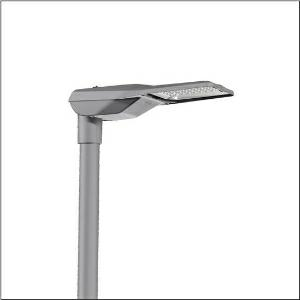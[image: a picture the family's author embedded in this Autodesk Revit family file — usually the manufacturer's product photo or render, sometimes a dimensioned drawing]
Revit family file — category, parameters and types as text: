
# Revit family: streetlight_sl_21_mini___st0_5a_5xe2b43s08gb_d1ce
name_source: partatom
category: Lighting Fixtures
units: mm (PartAtom-declared; Revit-internal decimal feet)

## family parameters
Cut with Voids When Loaded = No
Host = Face
Light Source = No
Part Type = Normal
Room Calculation Point = No
Round Connector Dimension = Use Diameter
Shared = No

## types (1)
- --- (1 x LED, 6180 lm, 40.4 W, 4000K)
    Apparent Load = 40 VA
    CIE Flux Codes = 41 75 97 100 100
    Color Rendering = 70
    Color Temperature = 4000K
    Default Elevation = 1800 mm
    Description = Streetlight SL 21 mini, mast luminaire, primary light control with lens, of PMMA, primary optical cover: cover, of toughened safety glass, transparent, light distribution: ST0.5a, light emission: direct distribution, primary light characteristic: asymmetric, installation type: side-entry, post-top, LED, High Power LED, rated luminous flux: 6.180lm, luminous efficacy: 153lm/W, light colour: 740, colour temperature: 4000K, control gear: ECG Smart Interface, control: overheat protection, constant luminous flux control, time-dependent luminous flux control, flexible luminous flux parameterisation, mains connection: 220..240V, AC, 50/60Hz, start of lifetime: 40W, end of lifetime: 41W, reduction: 19W, luminaire housing, of diecast aluminium, powder-coated, Siteco® metallic grey (DB 702S), corrosivity category C5 according to DIN EN ISO 12944, length: 628mm, width: 235mm, height: 110mm, spigot size: 60/76mm (post-top) and 42/60/76mm (side-entry), mast flange for spigot size: 42mm: 5XC10008XM4, 60mm: 5XC10008XM2, 76/60mm: 5XC10108XM1, protection rating (complete): IP66, insulation class (complete): insulation class II (safety insulation), certification: CE, ENEC, VDE, impact resistance: IK09, permissible operating ambient temperature for outdoor applications: -40..+50°C, standard-compliant lighting for roads and squares, packaging unit: 1 piece

Light Distribution: ST0.5a
    Height = 110 mm
    Lamp = 1 x LED
    Lamp Light Flux = 6180 lm
    Lamp Power = 40.4 W
    Lamp count = 1
    Length = 625 mm
    Luminous efficacy = 153 lm/W
    Manufacturer = Siteco
    ModVariant = No
    Model = 5XE2B43S08GB
    Number of Poles = 1
    OnlyDefault = Yes
    Power Factor = 1
    Product Name = Streetlight SL 21 mini | ST0.5a
    Product group = mast luminaire | pylon top
    ProductGroupID = 6100
    Protection Class = Protection class II
    Protection Degree = IP 66
    RLX_Detail_Level = 1
    RlxData = <blob elided: 102897 chars, md5=b4984032>
    Socket = socket
    Standby Power = 0 W
    System Light Flux = 6180 lm
    System Power = 40 W
    Type Comments = factory setting: luminous flux: 100 % | dim-lin: 254 | 812 mA
    Type Image = l_1003515.jpg
    URL = http://relux.com
    VarID = @adj_111187
    Voltage = 0 V
    Weight = 0.00 kg
    Width = 234 mm

## geometry (parser evidence)
native form markers: Blend x4, Sweep x9
no freeform markers — native parametric forms only
